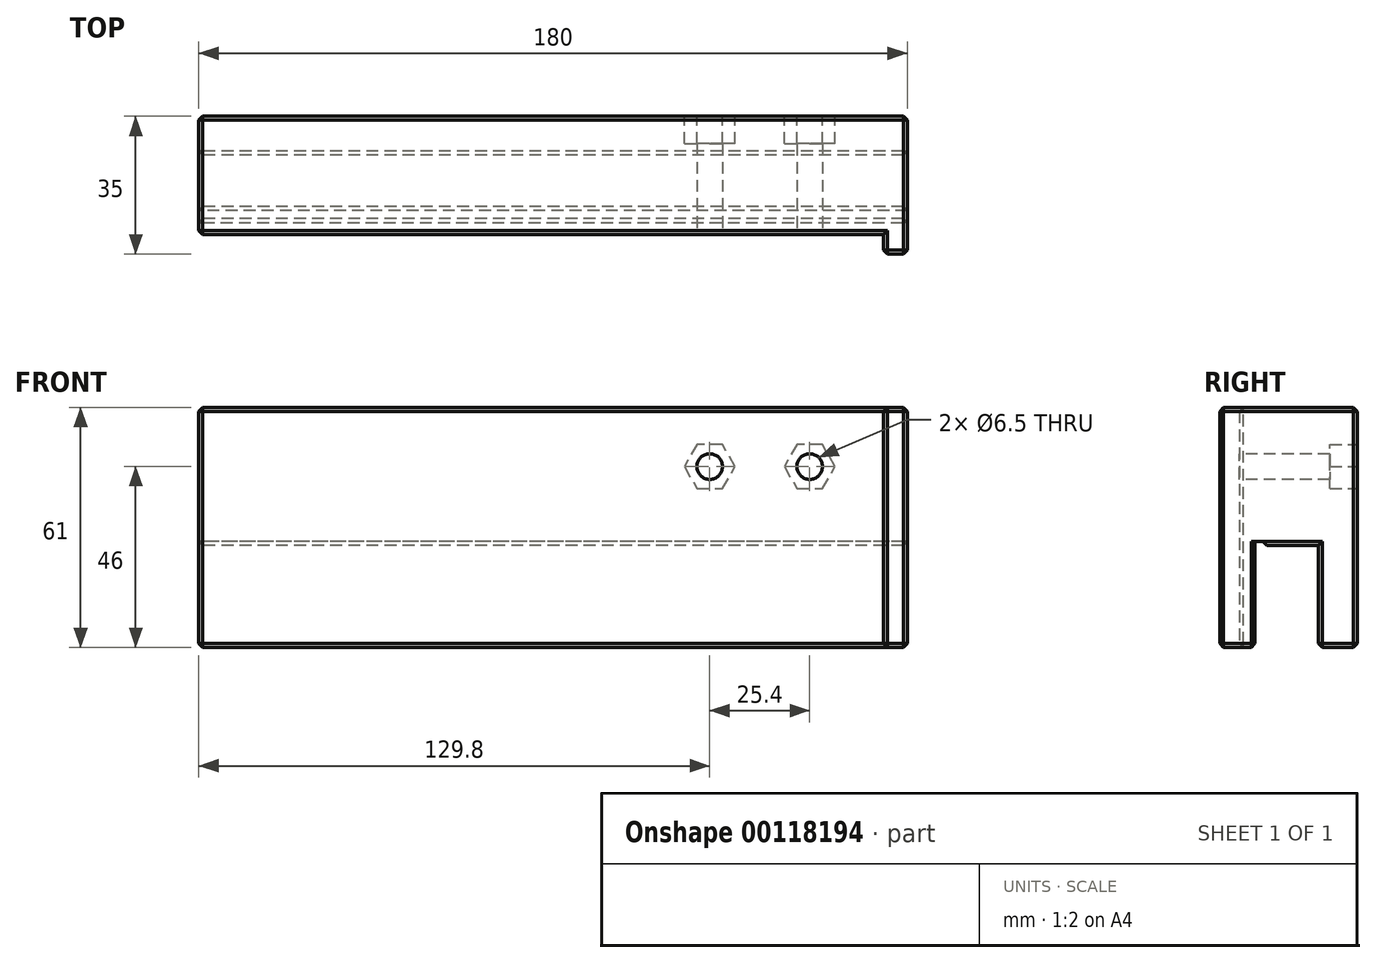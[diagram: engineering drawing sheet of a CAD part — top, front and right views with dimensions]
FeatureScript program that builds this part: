
annotation { "Feature Type Name" : "Feature", "Feature Type Description" : "" }
export const myFeature = defineFeature(function(context is Context, id is Id, definition is map)
    precondition{}
    {
        {
            var Q0;
            Q0=qCreatedBy(makeId("Right.planeOp"),FACE);
            var sketch = newSketch(context, id + "F0", { "sketchPlane" : qUnion([Q0])});
            skLineSegment(sketch, "E0.bottom", {"start": v(8.05, 13) * mm, "end": v(-6.05, 13) * mm});
            skLineSegment(sketch, "E0.top", {"start": v(8.05, -13) * mm, "end": v(-8.05, -13) * mm, "construction": true});
            skLineSegment(sketch, "E0.left", {"start": v(8.05, 13) * mm, "end": v(8.05, -13) * mm});
            skLineSegment(sketch, "E0.right", {"start": v(-8.05, 14) * mm, "end": v(-8.05, -13) * mm});
            skPoint(sketch, "E0.middle", {"position": v(0, 0) * mm});
            skLineSegment(sketch, "E1", {"start": v(8.05, -13) * mm, "end": v(17.95, -13) * mm});
            skLineSegment(sketch, "E2", {"start": v(17.95, -13) * mm, "end": v(17.95, 48) * mm});
            skLineSegment(sketch, "E3", {"start": v(17.95, 48) * mm, "end": v(-12.05, 48) * mm});
            skLineSegment(sketch, "E4", {"start": v(-12.05, 48) * mm, "end": v(-12.05, -13) * mm});
            skLineSegment(sketch, "E5", {"start": v(-12.05, -13) * mm, "end": v(-8.05, -13) * mm});
            skLineSegment(sketch, "E6", {"start": v(-6.05, 13) * mm, "end": v(-6.05, 14) * mm});
            skLineSegment(sketch, "E7", {"start": v(-6.05, 14) * mm, "end": v(-8.05, 14) * mm});
            skPoint(sketch, "E8.orphan", {"position": v(-8.05, 13) * mm});
            skSolve(sketch);
        }
        {
            var Q0;
            Q0 = qSketchRegion(id + "F0", true);
            extrude(context, id + "F1", {"entities" : qUnion([Q0]), "endBound" : BoundingType.SYMMETRIC, "depth" : 180 * mm});
        }
        {
            var Q0;
            Q0=makeQuery(id+"F1.opExtrude","SWEPT_FACE",FACE,{"disambiguationData":[OSD([sQuery(id+"F0.wireOp",EDGE,"E4")])]});
            var sketch = newSketch(context, id + "F2", { "sketchPlane" : qUnion([Q0])});
            skLineSegment(sketch, "E9.bottom", {"start": v(90, 48) * mm, "end": v(84, 48) * mm});
            skLineSegment(sketch, "E9.top", {"start": v(90, -13) * mm, "end": v(84, -13) * mm});
            skLineSegment(sketch, "E9.left", {"start": v(90, 48) * mm, "end": v(90, -13) * mm});
            skLineSegment(sketch, "E9.right", {"start": v(84, 48) * mm, "end": v(84, -13) * mm});
            skSolve(sketch);
        }
        {
            var Q0;
            Q0 = qSketchRegion(id + "F2", true);
            extrude(context, id + "F3", {"entities" : qUnion([Q0]), "operationType" : NewBodyOperationType.ADD, "depth" : 5 * mm});
        }
        {
            var Q0;
            Q0=makeQuery(id+"F1.opExtrude","SWEPT_FACE",FACE,{"disambiguationData":[OSD([sQuery(id+"F0.wireOp",EDGE,"E4")])]});
            var sketch = newSketch(context, id + "F4", { "sketchPlane" : qUnion([Q0])});
            skLineSegment(sketch, "E10", {"start": v(84, 33) * mm, "end": v(65.2, 33) * mm, "construction": true});
            skLineSegment(sketch, "E11", {"start": v(65.2, 33) * mm, "end": v(39.8, 33) * mm, "construction": true});
            skLineSegment(sketch, "E12", {"start": v(39.8, 33) * mm, "end": v(21, 33) * mm, "construction": true});
            skLineSegment(sketch, "E13", {"start": v(21, 33) * mm, "end": v(21, 48) * mm, "construction": true});
            skCircle(sketch, "E14", {"center": v(39.8, 33) * mm, "radius": 3.25 * mm});
            skCircle(sketch, "E15", {"center": v(65.2, 33) * mm, "radius": 3.25 * mm});
            skSolve(sketch);
        }
        {
            var Q0;
            Q0 = qSketchRegion(id + "F4", true);
            extrude(context, id + "F5", {"entities" : qUnion([Q0]), "operationType" : NewBodyOperationType.REMOVE, "endBound" : BoundingType.THROUGH_ALL, "oppositeDirection" : true, "depth" : 25 * mm});
        }
        {
            var Q0;
            Q0=makeQuery(id+"F1.opExtrude","SWEPT_FACE",FACE,{"disambiguationData":[OSD([sQuery(id+"F0.wireOp",EDGE,"E2")])]});
            var sketch = newSketch(context, id + "F6", { "sketchPlane" : qUnion([Q0])});
            skCircle(sketch, "E16.cCircle", {"center": v(-65.2, 33) * mm, "radius": 5.6 * mm, "construction": true});
            skLineSegment(sketch, "E16.0", {"start": v(-68.43, 38.6) * mm, "end": v(-61.97, 38.6) * mm});
            skLineSegment(sketch, "E16.1", {"start": v(-61.97, 38.6) * mm, "end": v(-58.73, 33) * mm});
            skLineSegment(sketch, "E16.2", {"start": v(-58.73, 33) * mm, "end": v(-61.97, 27.4) * mm});
            skLineSegment(sketch, "E16.3", {"start": v(-61.97, 27.4) * mm, "end": v(-68.43, 27.4) * mm});
            skLineSegment(sketch, "E16.4", {"start": v(-68.43, 27.4) * mm, "end": v(-71.67, 33) * mm});
            skLineSegment(sketch, "E16.5", {"start": v(-71.67, 33) * mm, "end": v(-68.43, 38.6) * mm});
            skPoint(sketch, "E16.0.midPoint", {"position": v(-65.2, 38.6) * mm});
            skCircle(sketch, "E17.cCircle", {"center": v(-39.8, 33) * mm, "radius": 5.6 * mm, "construction": true});
            skLineSegment(sketch, "E17.0", {"start": v(-43.03, 38.6) * mm, "end": v(-36.57, 38.6) * mm});
            skLineSegment(sketch, "E17.1", {"start": v(-36.57, 38.6) * mm, "end": v(-33.33, 33) * mm});
            skLineSegment(sketch, "E17.2", {"start": v(-33.33, 33) * mm, "end": v(-36.57, 27.4) * mm});
            skLineSegment(sketch, "E17.3", {"start": v(-36.57, 27.4) * mm, "end": v(-43.03, 27.4) * mm});
            skLineSegment(sketch, "E17.4", {"start": v(-43.03, 27.4) * mm, "end": v(-46.27, 33) * mm});
            skLineSegment(sketch, "E17.5", {"start": v(-46.27, 33) * mm, "end": v(-43.03, 38.6) * mm});
            skPoint(sketch, "E17.0.midPoint", {"position": v(-39.8, 38.6) * mm});
            skSolve(sketch);
        }
        {
            var Q0;
            Q0 = qSketchRegion(id + "F6", true);
            extrude(context, id + "F7", {"entities" : qUnion([Q0]), "operationType" : NewBodyOperationType.REMOVE, "oppositeDirection" : true, "depth" : 7 * mm});
        }
        {
            var Q0;
            Q0=makeQuery(id+"F1.opExtrude","SWEPT_EDGE",EDGE,{"disambiguationData":[OSD([sQuery(id+"F0.wireOp",EDGE,"E0.bottom"),sQuery(id+"F0.wireOp",EDGE,"E6")])]});
            chamfer(context, id + "F8", {"entities" : qUnion([Q0]), "width" : 1 * mm, "tangentPropagation" : true});
        }
        {
            var Q0;
            Q0=makeQuery(id+"F1.opExtrude","SWEPT_EDGE",EDGE,{"disambiguationData":[OSD([sQuery(id+"F0.wireOp",EDGE,"E0.right"),sQuery(id+"F0.wireOp",EDGE,"E5")])]});
            var Q1;
            Q1=makeQuery(id+"F1.opExtrude","SWEPT_EDGE",EDGE,{"disambiguationData":[OSD([sQuery(id+"F0.wireOp",EDGE,"E0.left"),sQuery(id+"F0.wireOp",EDGE,"E1")])]});
            var Q2;
            Q2=makeQuery(id+"F1.opExtrude","SWEPT_EDGE",EDGE,{"disambiguationData":[OSD([sQuery(id+"F0.wireOp",EDGE,"E1"),sQuery(id+"F0.wireOp",EDGE,"E2")])]});
            var Q3;
            Q3=makeQuery(id+"F1.opExtrude","CAP_EDGE",EDGE,{"disambiguationData":[OSD([sQuery(id+"F0.wireOp",EDGE,"E1")])],"isStart":true});
            var Q4;
            Q4=makeQuery(id+"F1.opExtrude","CAP_EDGE",EDGE,{"disambiguationData":[OSD([sQuery(id+"F0.wireOp",EDGE,"E0.left")])],"isStart":true});
            var Q5;
            Q5=makeQuery(id+"F1.opExtrude","CAP_EDGE",EDGE,{"disambiguationData":[OSD([sQuery(id+"F0.wireOp",EDGE,"E1")])],"isStart":false});
            var Q6;
            Q6=makeQuery(id+"F1.opExtrude","SWEPT_EDGE",EDGE,{"disambiguationData":[OSD([sQuery(id+"F0.wireOp",EDGE,"E4"),sQuery(id+"F0.wireOp",EDGE,"E5")])]});
            var Q7;
            Q7=makeQuery(id+"F1.opExtrude","CAP_EDGE",EDGE,{"disambiguationData":[OSD([sQuery(id+"F0.wireOp",EDGE,"E5")])],"isStart":true});
            var Q8;
            Q8=makeQuery(id+"F3.opExtrude","SWEPT_EDGE",EDGE,{"disambiguationData":[OSD([sQuery(id+"F0.wireOp",EDGE,"E4"),sQuery(id+"F0.wireOp",EDGE,"E5"),sQuery(id+"F2.wireOp",EDGE,"E9.top"),sQuery(id+"F2.wireOp",EDGE,"E9.right")])]});
            var Q9;
            Q9=makeQuery(id+"F3.boolean.opBoolean","MERGE",EDGE,{"derivedFrom":[makeQuery(id+"F1.opExtrude","CAP_EDGE",EDGE,{"disambiguationData":[OSD([sQuery(id+"F0.wireOp",EDGE,"E5")])],"isStart":false}),makeQuery(id+"F3.opExtrude","SWEPT_EDGE",EDGE,{"disambiguationData":[OSD([sQuery(id+"F2.wireOp",EDGE,"E9.top"),sQuery(id+"F2.wireOp",EDGE,"E9.left")])]})]});
            var Q10;
            Q10=makeQuery(id+"F3.opExtrude","CAP_EDGE",EDGE,{"disambiguationData":[OSD([sQuery(id+"F2.wireOp",EDGE,"E9.top")])],"isStart":false});
            var Q11;
            Q11=makeQuery(id+"F1.opExtrude","CAP_EDGE",EDGE,{"disambiguationData":[OSD([sQuery(id+"F0.wireOp",EDGE,"E4")])],"isStart":true});
            var Q12;
            Q12=makeQuery(id+"F1.opExtrude","CAP_EDGE",EDGE,{"disambiguationData":[OSD([sQuery(id+"F0.wireOp",EDGE,"E2")])],"isStart":true});
            var Q13;
            Q13=makeQuery(id+"F1.opExtrude","CAP_EDGE",EDGE,{"disambiguationData":[OSD([sQuery(id+"F0.wireOp",EDGE,"E0.right")])],"isStart":true});
            var Q14;
            Q14=makeQuery(id+"F1.opExtrude","CAP_EDGE",EDGE,{"disambiguationData":[OSD([sQuery(id+"F0.wireOp",EDGE,"E0.left")])],"isStart":false});
            var Q15;
            Q15=makeQuery(id+"F1.opExtrude","CAP_EDGE",EDGE,{"disambiguationData":[OSD([sQuery(id+"F0.wireOp",EDGE,"E0.right")])],"isStart":false});
            var Q16;
            Q16=makeQuery(id+"F1.opExtrude","CAP_EDGE",EDGE,{"disambiguationData":[OSD([sQuery(id+"F0.wireOp",EDGE,"E0.bottom")])],"isStart":false});
            var Q17;
            Q17=makeQuery(id+"F1.opExtrude","CAP_EDGE",EDGE,{"disambiguationData":[OSD([sQuery(id+"F0.wireOp",EDGE,"E0.bottom")])],"isStart":true});
            var Q18;
            Q18=makeQuery(id+"F3.boolean.opBoolean","MERGE",EDGE,{"derivedFrom":[makeQuery(id+"F1.opExtrude","CAP_EDGE",EDGE,{"disambiguationData":[OSD([sQuery(id+"F0.wireOp",EDGE,"E3")])],"isStart":false}),makeQuery(id+"F3.opExtrude","SWEPT_EDGE",EDGE,{"disambiguationData":[OSD([sQuery(id+"F2.wireOp",EDGE,"E9.bottom"),sQuery(id+"F2.wireOp",EDGE,"E9.left")])]})]});
            var Q19;
            Q19=makeQuery(id+"F1.opExtrude","CAP_EDGE",EDGE,{"disambiguationData":[OSD([sQuery(id+"F0.wireOp",EDGE,"E2")])],"isStart":false});
            var Q20;
            Q20=makeQuery(id+"F1.opExtrude","SWEPT_EDGE",EDGE,{"disambiguationData":[OSD([sQuery(id+"F0.wireOp",EDGE,"E2"),sQuery(id+"F0.wireOp",EDGE,"E3")])]});
            var Q21;
            Q21=makeQuery(id+"F1.opExtrude","SWEPT_EDGE",EDGE,{"disambiguationData":[OSD([sQuery(id+"F0.wireOp",EDGE,"E3"),sQuery(id+"F0.wireOp",EDGE,"E4")])]});
            var Q22;
            Q22=makeQuery(id+"F1.opExtrude","CAP_EDGE",EDGE,{"disambiguationData":[OSD([sQuery(id+"F0.wireOp",EDGE,"E3")])],"isStart":true});
            var Q23;
            Q23=makeQuery(id+"F3.opExtrude","CAP_EDGE",EDGE,{"disambiguationData":[OSD([sQuery(id+"F2.wireOp",EDGE,"E9.bottom")])],"isStart":false});
            var Q24;
            Q24=makeQuery(id+"F3.opExtrude","SWEPT_EDGE",EDGE,{"disambiguationData":[OSD([sQuery(id+"F0.wireOp",EDGE,"E3"),sQuery(id+"F0.wireOp",EDGE,"E4"),sQuery(id+"F2.wireOp",EDGE,"E9.bottom"),sQuery(id+"F2.wireOp",EDGE,"E9.right")])]});
            var Q25;
            Q25=makeQuery(id+"F3.opExtrude","CAP_EDGE",EDGE,{"disambiguationData":[OSD([sQuery(id+"F2.wireOp",EDGE,"E9.left")])],"isStart":false});
            var Q26;
            Q26=makeQuery(id+"F3.opExtrude","CAP_EDGE",EDGE,{"disambiguationData":[OSD([sQuery(id+"F2.wireOp",EDGE,"E9.right")])],"isStart":false});
            chamfer(context, id + "F9", {"entities" : qUnion([Q0, Q1, Q2, Q3, Q4, Q5, Q6, Q7, Q8, Q9, Q10, Q11, Q12, Q13, Q14, Q15, Q16, Q17, Q18, Q19, Q20, Q21, Q22, Q23, Q24, Q25, Q26]), "width" : 1 * mm, "tangentPropagation" : true});
        }
    });
